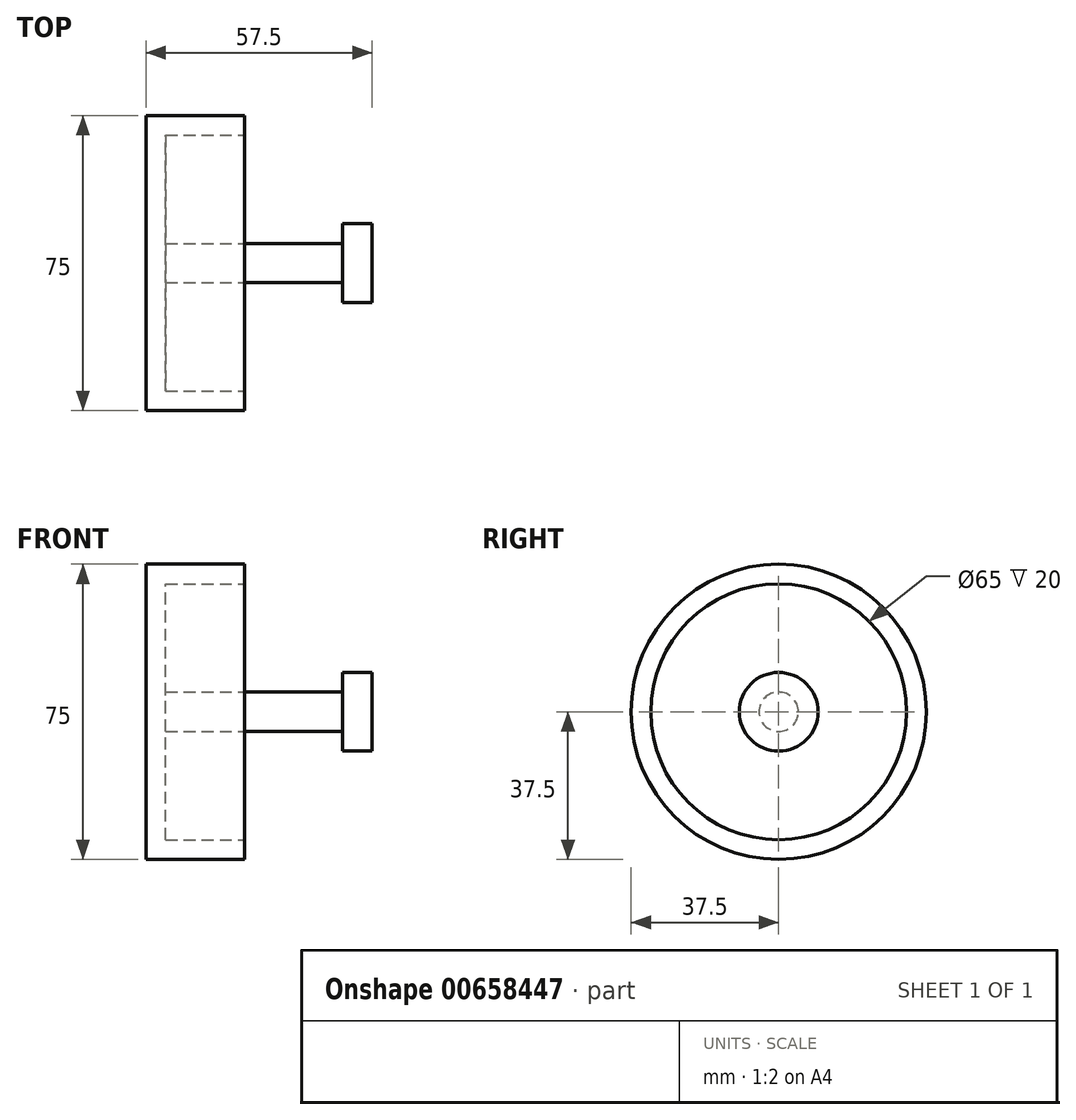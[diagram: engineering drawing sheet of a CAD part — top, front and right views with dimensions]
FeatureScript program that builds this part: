
annotation { "Feature Type Name" : "Feature", "Feature Type Description" : "" }
export const myFeature = defineFeature(function(context is Context, id is Id, definition is map)
    precondition{}
    {
        {
            var Q0;
            Q0=qCreatedBy(makeId("Front.planeOp"),FACE);
            var sketch = newSketch(context, id + "F0", { "sketchPlane" : qUnion([Q0])});
            skLineSegment(sketch, "E0", {"start": v(0, 0) * mm, "end": v(0, 37.5) * mm});
            skLineSegment(sketch, "E1", {"start": v(0, 37.5) * mm, "end": v(25, 37.5) * mm});
            skLineSegment(sketch, "E2", {"start": v(25, 37.5) * mm, "end": v(25, 32.5) * mm});
            skLineSegment(sketch, "E3", {"start": v(25, 32.5) * mm, "end": v(5, 32.5) * mm});
            skLineSegment(sketch, "E4", {"start": v(5, 32.5) * mm, "end": v(5, 5) * mm});
            skLineSegment(sketch, "E5", {"start": v(5, 5) * mm, "end": v(50, 5) * mm});
            skLineSegment(sketch, "E6", {"start": v(50, 5) * mm, "end": v(50, 10) * mm});
            skLineSegment(sketch, "E7", {"start": v(50, 10) * mm, "end": v(57.5, 10) * mm});
            skLineSegment(sketch, "E8", {"start": v(57.5, 10) * mm, "end": v(57.5, 0) * mm});
            skLineSegment(sketch, "E9", {"start": v(57.5, 0) * mm, "end": v(0, 0) * mm});
            skSolve(sketch);
        }
        {
            var Q0;
            Q0=makeQuery(id+"F0.imprint","IMPRINT",FACE,{"disambiguationData":[TD([[makeQuery(id+"F0.imprint","IMPRINT",EDGE,{"derivedFrom":sQuery(id+"F0.wireOp",EDGE,"E0")}),-1.0]])]});
            var Q1;
            Q1=sQuery(id+"F0.wireOp",EDGE,"E9");
            revolve(context, id + "F1", {"entities" : qUnion([Q0]), "axis" : qUnion([Q1]), "revolveType" : RevolveType.FULL});
        }
    });
